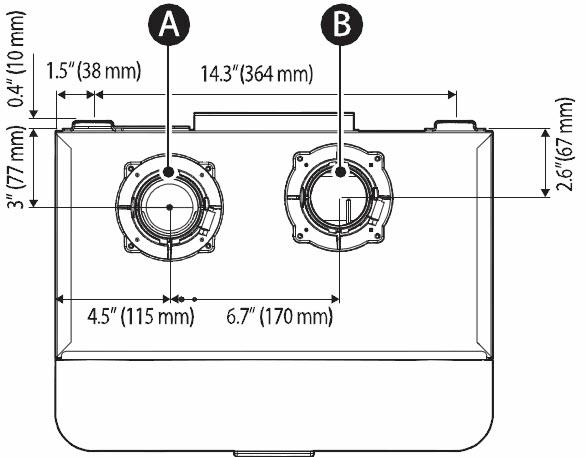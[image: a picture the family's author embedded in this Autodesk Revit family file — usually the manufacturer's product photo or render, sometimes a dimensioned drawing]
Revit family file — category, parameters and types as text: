
# Revit family: Water_Heater-Racks-Navien-NPE-16_Unit_Back_to_Back---
name_source: partatom
category: Mechanical Equipment
revit_build: Autodesk Revit 2016 (Build: 20150220_1215(x64)
units: mm (PartAtom-declared; Revit-internal decimal feet)

## family parameters
Cut with Voids When Loaded = No
Host = Face
OmniClass Number = 23.65.35.11
OmniClass Title = Supply Water Heaters
Part Type = Normal
Room Calculation Point = No
Round Connector Dimension = Use Diameter
Shared = No

## types (4) — shared parameters
2" Exhaust/Intake = Yes
3" Exhaust/Intake = No
Apparent Load = 0 VA
Assembly Code = D3010500
Certifications = Energy Star | AHRI | CSA | CSA | NFS
Cold Water Inlet = 1"
Configuration = NPE_B16_4B4B_4B4B
Default Elevation = 48 "
Depth = 23.8 "
Description = 16 Unit Back to Back
Exhaust = 2"
Finish = Metal - Navien - White
Flow Rate = 1 GPM
Flow Rate Note = 35°F (19°C) temp rise: 11.2 GPM (42 L/m) | 45°F (25°C) temp rise: 8.7 GPM (33 L/m) | 67°F (36°C) temp rise: NPE-240A: 5.6 GPM(21 L/m), NPE-240S: 5.7 GPM(22 L/m)
Frequency = 60 Hz
Gas Inlet = 1"
Heating Capacity = 120000.0 Btu/h
Heating Capacity Note = 19,900–199,900 (BTU/H)
Height = 65.5 "
Hot Water Outlet = 1"
Ignition = Electronic ignition
Installation Type = Indoor
Intake = 2"
Keynote = 22 33 00.A1
Manifold(s) = (4) 30019042A
Manufacturer = Navien, Inc.
Manufacturer Fax Number = (949) 420-0430
Natural Gas Manifold Pressure = -0.05" WC to -0.58" WC
Natural Gas Supply Pressure = 3.5"–10.5" WC
Number of Poles = 1
Phase = 1
Power Factor = 1
Product Documentation Link = https://www.navieninc.com
Product Name = NPE Series Tankless Water Heaters w/ Racks
Product Page URL = https://www.navieninc.com
Propane Gas Manifold Pressure = -0.10" WC to -0.78" WC
Propane Gas Supply Pressure = 8"–13" WC
Rack(s) = (2) GFFM-KDIZUS-003 + (6) GFFM-KDIZUS-004
Required Cascade Operation Accessory = (16) 30014367A (Common Vent Damper & Cascade Communication Cable) or (15) GXXX000546 (Individual Vent Cascade Communication Cable)
URL = https://www.navieninc.com
Venting = Exhaust: 2" PVC, CPVC, PP, SS / 2" special gas vent type BH (Class II, A/B/C) | Intake: 2" PVC, CPVC, PP, SS / 2" special gas vent type BH (Class II, A/B/C) | Vent clearances: 0" to combustibles
Venting Type = Forced draft direct vent
Version = 2016 - v1.0.a
Voltage = 120 V
Water Pressure = 15–150 PSI
Wi-Fi Ready = NaviLink Wi-Fi Control: PBCM-AS-001
Width = 182.3 "

## per-type parameters (varying)
| type | Constraints | Model | Natural Gas | Propane Gas | Recirculation Inlet | Recirculation Inlet Visibility | Tankless Water Heaters | Weight |
| Natural Gas - Recirculating System - NPE-240A(Advanced)-NG | 6 | (16) NPE-240A-NG | Yes | No | 0" | Yes | (16) NPE-240A-NG | 82.00 lbf |
| Natural Gas - NPE-240S(Standard)-NG | 7 | (16) NPE-240S-NG | Yes | No | 1" | No | (16) NPE-240S-NG | 75.00 lbf |
| Propane Gas - Recirculating System - NPE-240A(Advanced)-LPG | 6 | (16) NPE-240A-LPG | No | Yes | 0" | Yes | (16) NPE-240A-LPG | 82.00 lbf |
| Propane Gas - NPE-240S(Standard)-LPG | 7 | (16) NPE-240S-LPG | No | Yes | 1" | No | (16) NPE-240S-LPG | 75.00 lbf |

## geometry (parser evidence)
native form markers: Sweep x16
no freeform markers — native parametric forms only
